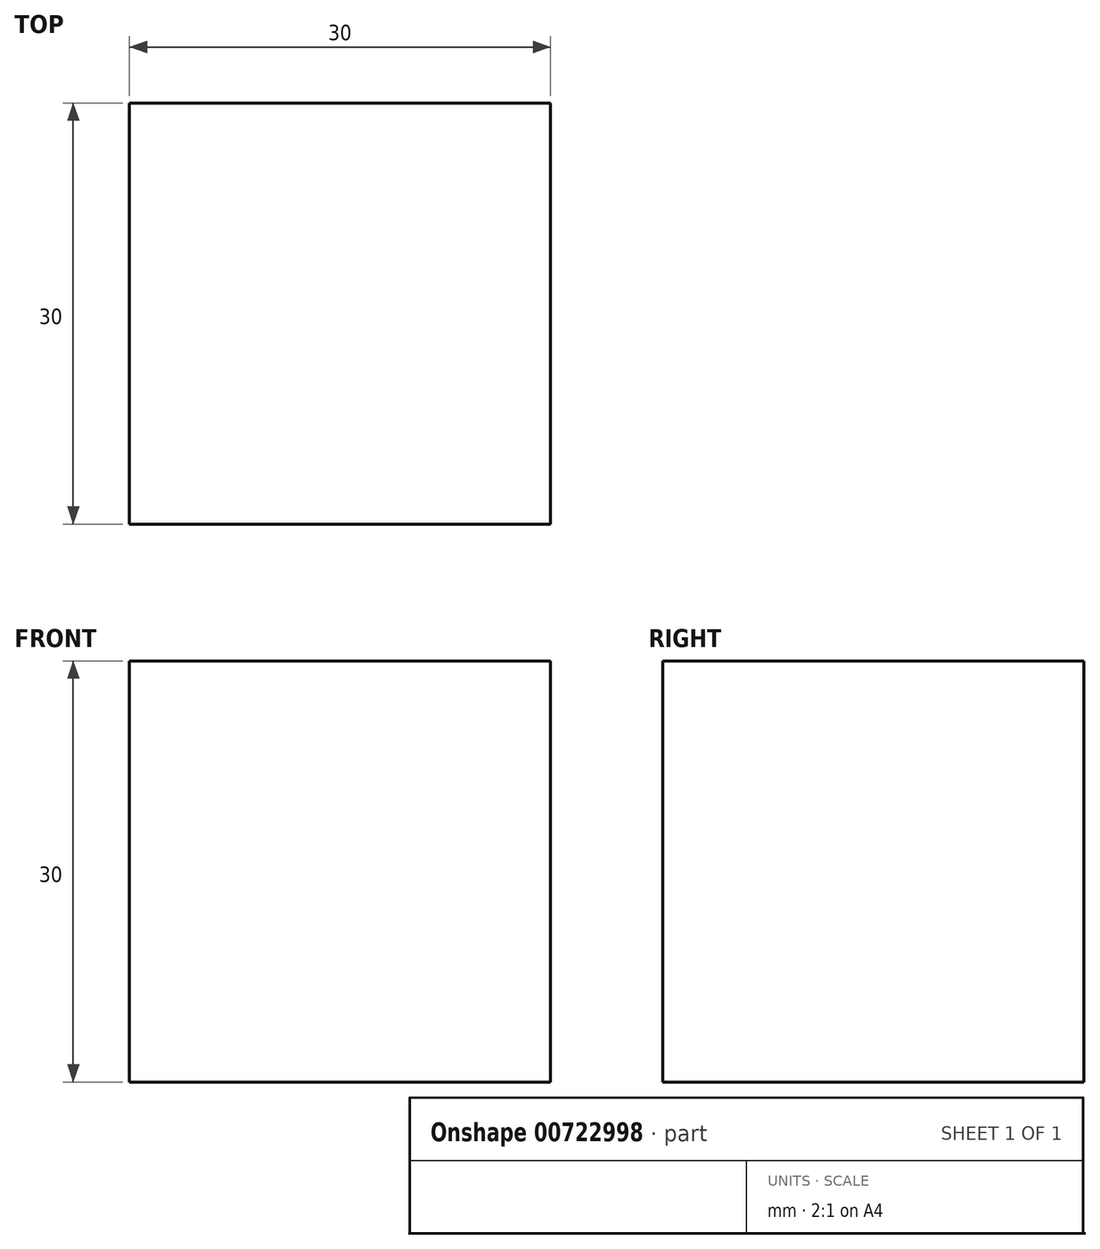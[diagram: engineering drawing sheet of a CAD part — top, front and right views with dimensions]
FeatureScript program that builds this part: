
annotation { "Feature Type Name" : "Feature", "Feature Type Description" : "" }
export const myFeature = defineFeature(function(context is Context, id is Id, definition is map)
    precondition{}
    {
        {
            var Q0;
            Q0=qCreatedBy(makeId("Front.planeOp"),FACE);
            var sketch = newSketch(context, id + "F0", { "sketchPlane" : qUnion([Q0])});
            skLineSegment(sketch, "E0.bottom", {"start": v(0, 0) * mm, "end": v(-30, 0) * mm});
            skLineSegment(sketch, "E0.top", {"start": v(0, 30) * mm, "end": v(-30, 30) * mm});
            skLineSegment(sketch, "E0.left", {"start": v(0, 0) * mm, "end": v(0, 30) * mm});
            skLineSegment(sketch, "E0.right", {"start": v(-30, 0) * mm, "end": v(-30, 30) * mm});
            skSolve(sketch);
        }
        {
            var Q0;
            Q0=makeQuery(id+"F0.imprint","IMPRINT",FACE,{"disambiguationData":[TD([[makeQuery(id+"F0.imprint","IMPRINT",EDGE,{"derivedFrom":sQuery(id+"F0.wireOp",EDGE,"E0.bottom")}),-1.0]])]});
            extrude(context, id + "F1", {"entities" : qUnion([Q0]), "depth" : 30 * mm, "offsetDistance" : 25 * mm});
        }
    });
